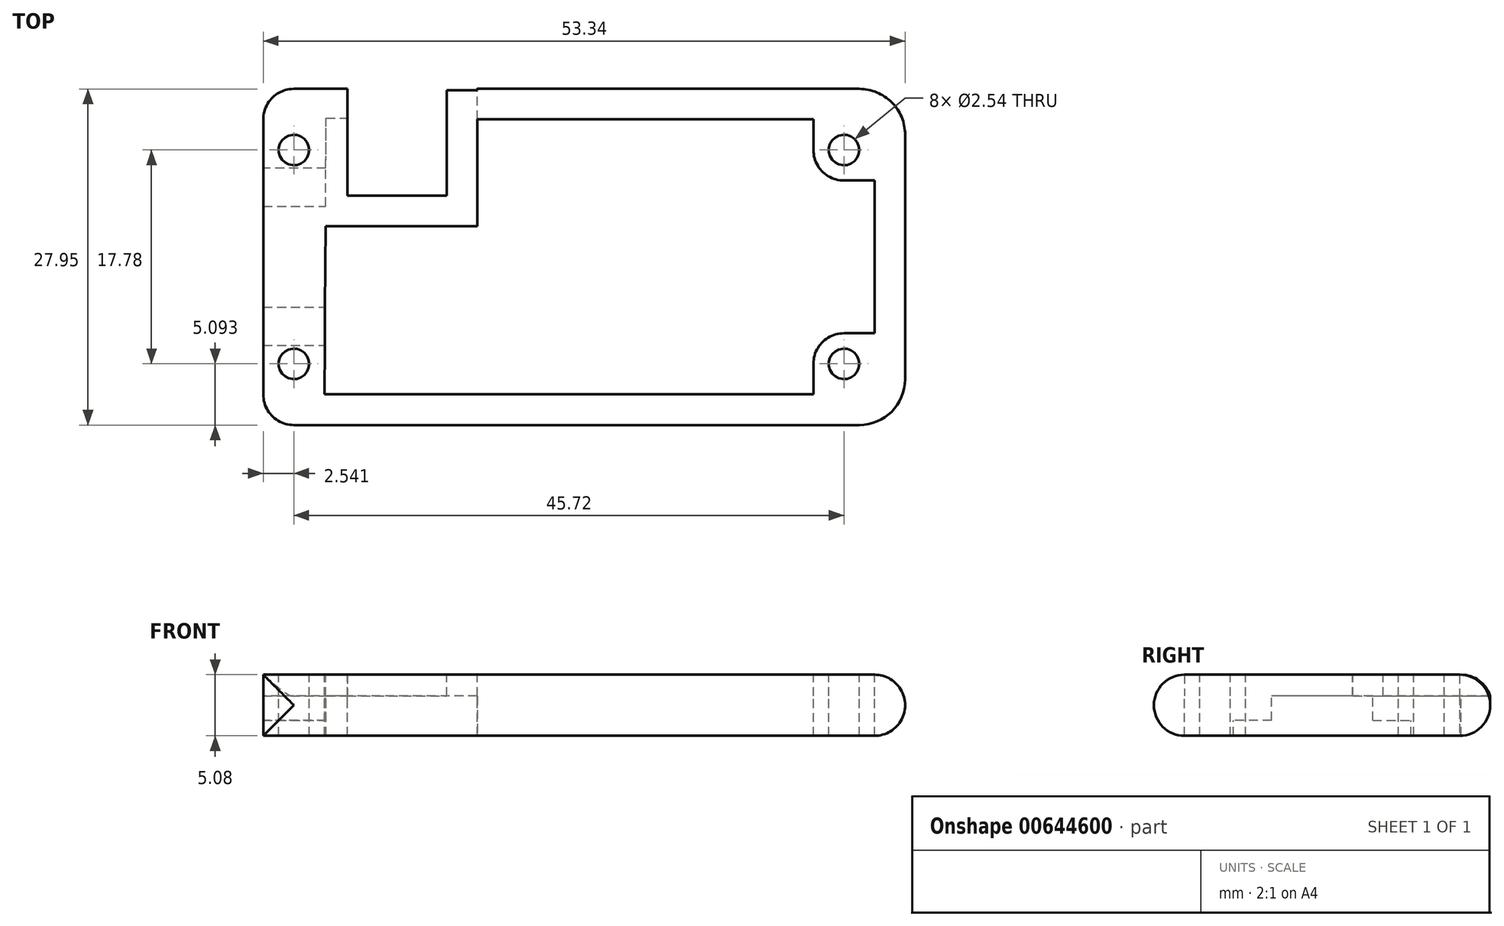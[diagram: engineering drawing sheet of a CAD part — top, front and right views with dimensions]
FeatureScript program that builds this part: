
annotation { "Feature Type Name" : "Feature", "Feature Type Description" : "" }
export const myFeature = defineFeature(function(context is Context, id is Id, definition is map)
    precondition{}
    {
        {
            var Q0;
            Q0=qCreatedBy(makeId("Top.planeOp"),FACE);
            var sketch = newSketch(context, id + "F0", { "sketchPlane" : qUnion([Q0])});
            skLineSegment(sketch, "E0", {"start": v(-27.7, 10.58) * mm, "end": v(-27.7, -12.28) * mm});
            skLineSegment(sketch, "E1", {"start": v(-25.17, -14.82) * mm, "end": v(21.82, -14.82) * mm});
            skLineSegment(sketch, "E2", {"start": v(-25.17, 13.12) * mm, "end": v(-20.72, 13.12) * mm});
            skLineSegment(sketch, "E3", {"start": v(-20.72, 13.12) * mm, "end": v(-20.72, 4.23) * mm});
            skLineSegment(sketch, "E4", {"start": v(-20.72, 4.23) * mm, "end": v(-12.47, 4.23) * mm});
            skLineSegment(sketch, "E5", {"start": v(-12.47, 4.23) * mm, "end": v(-12.47, 13.12) * mm});
            skLineSegment(sketch, "E6", {"start": v(23.1, 5.5) * mm, "end": v(23.1, -7.2) * mm});
            skLineSegment(sketch, "E7", {"start": v(18.01, -12.28) * mm, "end": v(-22.63, -12.28) * mm});
            skLineSegment(sketch, "E8", {"start": v(-9.93, 1.7) * mm, "end": v(-9.93, 10.58) * mm});
            skLineSegment(sketch, "E9", {"start": v(18.01, 10.58) * mm, "end": v(-9.93, 10.58) * mm});
            skPoint(sketch, "E10.visualSharp", {"position": v(-27.7, 13.12) * mm});
            skArc(sketch, "E10.filletArc", {"start": v(-25.17, 13.12) * mm, "mid": v(-26.97, 12.38) * mm, "end": v(-27.7, 10.58) * mm});
            skPoint(sketch, "E11.visualSharp", {"position": v(-27.7, -14.82) * mm});
            skArc(sketch, "E11.filletArc", {"start": v(-27.7, -12.28) * mm, "mid": v(-26.97, -14.07) * mm, "end": v(-25.17, -14.82) * mm});
            skPoint(sketch, "E12.visualSharp", {"position": v(25.63, -14.82) * mm});
            skArc(sketch, "E12.filletArc", {"start": v(21.82, -14.82) * mm, "mid": v(24.52, -13.7) * mm, "end": v(25.63, -11) * mm});
            skPoint(sketch, "E13.visualSharp", {"position": v(25.63, 13.12) * mm});
            skArc(sketch, "E13.filletArc", {"start": v(25.63, 9.31) * mm, "mid": v(24.52, 12) * mm, "end": v(21.82, 13.12) * mm});
            skCircle(sketch, "E14", {"center": v(20.55, 8.04) * mm, "radius": 1.27 * mm});
            skCircle(sketch, "E15", {"center": v(20.55, -9.74) * mm, "radius": 1.27 * mm});
            skCircle(sketch, "E16", {"center": v(-25.17, -9.74) * mm, "radius": 1.27 * mm});
            skCircle(sketch, "E17", {"center": v(-25.17, 8.04) * mm, "radius": 1.27 * mm});
            skLineSegment(sketch, "E18", {"start": v(18.01, 10.58) * mm, "end": v(18.01, 8.04) * mm});
            skLineSegment(sketch, "E19", {"start": v(20.55, 5.5) * mm, "end": v(23.1, 5.5) * mm});
            skLineSegment(sketch, "E20", {"start": v(18.01, -12.28) * mm, "end": v(18.01, -9.74) * mm});
            skLineSegment(sketch, "E21", {"start": v(20.55, -7.2) * mm, "end": v(23.1, -7.2) * mm});
            skPoint(sketch, "E22.visualSharp", {"position": v(18.01, -7.2) * mm});
            skArc(sketch, "E22.filletArc", {"start": v(20.55, -7.2) * mm, "mid": v(18.75, -7.94) * mm, "end": v(18.01, -9.74) * mm});
            skPoint(sketch, "E23.visualSharp", {"position": v(18.01, 5.5) * mm});
            skArc(sketch, "E23.filletArc", {"start": v(18.01, 8.04) * mm, "mid": v(18.75, 6.25) * mm, "end": v(20.55, 5.5) * mm});
            skLineSegment(sketch, "E24", {"start": v(-9.83, 1.71) * mm, "end": v(-22.53, 1.7) * mm});
            skLineSegment(sketch, "E25", {"start": v(-22.53, 1.7) * mm, "end": v(-22.63, -12.28) * mm});
            skLineSegment(sketch, "E26", {"start": v(25.63, -11) * mm, "end": v(25.63, 9.31) * mm});
            skLineSegment(sketch, "E27", {"start": v(-12.47, 13.12) * mm, "end": v(21.82, 13.12) * mm});
            skSolve(sketch);
        }
        {
            var Q0;
            Q0=makeQuery(id+"F0.imprint","IMPRINT",FACE,{"disambiguationData":[TD([[makeQuery(id+"F0.imprint","IMPRINT",EDGE,{"derivedFrom":sQuery(id+"F0.wireOp",EDGE,"E0")}),1.0]])]});
            extrude(context, id + "F1", {"entities" : qUnion([Q0]), "oppositeDirection" : true, "depth" : 1.78 * mm, "offsetDistance" : 25.4 * mm});
        }
        {
            var Q0;
            Q0=qCreatedBy(makeId("Top.planeOp"),FACE);
            var sketch = newSketch(context, id + "F2", { "sketchPlane" : qUnion([Q0])});
            skLineSegment(sketch, "E28", {"start": v(23.1, 5.5) * mm, "end": v(23.1, -7.2) * mm});
            skLineSegment(sketch, "E29", {"start": v(18.01, -12.28) * mm, "end": v(-22.63, -12.28) * mm});
            skPoint(sketch, "E30.visualSharp", {"position": v(-27.7, 13.11) * mm});
            skPoint(sketch, "E31.visualSharp", {"position": v(-27.7, -14.83) * mm});
            skPoint(sketch, "E32.visualSharp", {"position": v(25.63, -14.83) * mm});
            skCircle(sketch, "E33", {"center": v(20.55, 8.04) * mm, "radius": 1.27 * mm});
            skCircle(sketch, "E34", {"center": v(20.55, -9.74) * mm, "radius": 1.27 * mm});
            skCircle(sketch, "E35", {"center": v(-25.17, -9.74) * mm, "radius": 1.27 * mm});
            skCircle(sketch, "E36", {"center": v(-25.17, 8.04) * mm, "radius": 1.27 * mm});
            skLineSegment(sketch, "E37", {"start": v(18.01, 10.58) * mm, "end": v(18.01, 8.04) * mm});
            skLineSegment(sketch, "E38", {"start": v(20.55, 5.5) * mm, "end": v(23.1, 5.5) * mm});
            skLineSegment(sketch, "E39", {"start": v(18.01, -12.28) * mm, "end": v(18.01, -9.74) * mm});
            skLineSegment(sketch, "E40", {"start": v(20.55, -7.2) * mm, "end": v(23.1, -7.2) * mm});
            skPoint(sketch, "E41.visualSharp", {"position": v(18.01, -7.2) * mm});
            skArc(sketch, "E41.filletArc", {"start": v(20.55, -7.2) * mm, "mid": v(18.75, -7.94) * mm, "end": v(18.01, -9.74) * mm});
            skPoint(sketch, "E42.visualSharp", {"position": v(18.01, 5.5) * mm});
            skArc(sketch, "E42.filletArc", {"start": v(18.01, 8.04) * mm, "mid": v(18.75, 6.25) * mm, "end": v(20.55, 5.5) * mm});
            skLineSegment(sketch, "E43", {"start": v(-27.7, -5.04) * mm, "end": v(-22.58, -5.04) * mm});
            skLineSegment(sketch, "E44", {"start": v(-22.58, -5.04) * mm, "end": v(-22.63, -12.28) * mm});
            skLineSegment(sketch, "E45", {"start": v(-22.5, 10.69) * mm, "end": v(-20.72, 10.68) * mm});
            skLineSegment(sketch, "E46", {"start": v(-20.72, 10.68) * mm, "end": v(-20.72, 13.11) * mm});
            skLineSegment(sketch, "E47", {"start": v(-27.7, 3.35) * mm, "end": v(-22.53, 3.35) * mm});
            skLineSegment(sketch, "E48", {"start": v(-22.53, 3.35) * mm, "end": v(-22.5, 10.69) * mm});
            skLineSegment(sketch, "E49", {"start": v(18.01, 10.58) * mm, "end": v(-9.93, 10.58) * mm});
            skLineSegment(sketch, "E50", {"start": v(-9.93, 10.58) * mm, "end": v(-9.93, 13.12) * mm});
            skLineSegment(sketch, "E51", {"start": v(-22.51, 6.53) * mm, "end": v(-27.7, 6.53) * mm});
            skLineSegment(sketch, "E52", {"start": v(-27.7, -5.04) * mm, "end": v(-27.7, -8.21) * mm});
            skLineSegment(sketch, "E53", {"start": v(-27.7, -8.21) * mm, "end": v(-22.6, -8.21) * mm});
            skLineSegment(sketch, "E54", {"start": v(-27.7, 3.35) * mm, "end": v(-27.7, 10.57) * mm});
            skLineSegment(sketch, "E55", {"start": v(-20.72, 13.11) * mm, "end": v(-25.17, 13.11) * mm});
            skArc(sketch, "E56.filletArc", {"start": v(-25.17, 13.11) * mm, "mid": v(-26.97, 12.37) * mm, "end": v(-27.7, 10.57) * mm});
            skLineSegment(sketch, "E57", {"start": v(-27.7, -5.04) * mm, "end": v(-27.7, -12.29) * mm});
            skArc(sketch, "E58.filletArc", {"start": v(-27.7, -12.29) * mm, "mid": v(-26.97, -14.09) * mm, "end": v(-25.17, -14.83) * mm});
            skLineSegment(sketch, "E59", {"start": v(25.63, 10.58) * mm, "end": v(25.63, 10.58) * mm});
            skLineSegment(sketch, "E60", {"start": v(23.08, 13.12) * mm, "end": v(23.1, 13.12) * mm});
            skPoint(sketch, "E61.visualSharp", {"position": v(25.63, 13.12) * mm});
            skLineSegment(sketch, "E62", {"start": v(-25.17, -14.83) * mm, "end": v(21.82, -14.83) * mm});
            skLineSegment(sketch, "E63", {"start": v(25.63, -11.02) * mm, "end": v(25.63, 9.31) * mm});
            skLineSegment(sketch, "E64", {"start": v(21.82, 13.12) * mm, "end": v(-9.93, 13.12) * mm});
            skArc(sketch, "E65.filletArc", {"start": v(21.82, -14.83) * mm, "mid": v(24.52, -13.71) * mm, "end": v(25.63, -11.02) * mm});
            skArc(sketch, "E66.filletArc", {"start": v(25.63, 9.31) * mm, "mid": v(24.52, 12) * mm, "end": v(21.82, 13.12) * mm});
            skSolve(sketch);
        }
        {
            var Q0;
            Q0=makeQuery(id+"F2.imprint","IMPRINT",FACE,{"disambiguationData":[TD([[makeQuery(id+"F2.imprint","IMPRINT",EDGE,{"derivedFrom":sQuery(id+"F2.wireOp",EDGE,"E28")}),1.0]])]});
            var Q1;
            Q1=makeQuery(id+"F2.imprint","IMPRINT",FACE,{"disambiguationData":[TD([[makeQuery(id+"F2.imprint","IMPRINT",EDGE,{"derivedFrom":sQuery(id+"F2.wireOp",EDGE,"E36")}),-1.0]])]});
            extrude(context, id + "F3", {"entities" : qUnion([Q0, Q1]), "operationType" : NewBodyOperationType.ADD, "oppositeDirection" : true, "depth" : 5.08 * mm, "offsetDistance" : 25.4 * mm});
        }
        {
            var Q0;
            {var subQ0=sQuery(id+"F2.wireOp",EDGE,"E47");Q0=makeQuery(id+"F2.imprint","IMPRINT",FACE,{"disambiguationData":[TD([[makeQuery(id+"F2.imprint","IMPRINT",EDGE,{"derivedFrom":subQ0}),1.0]])]});}
            var Q1;
            {var subQ0=sQuery(id+"F2.wireOp",EDGE,"E43");Q1=makeQuery(id+"F2.imprint","IMPRINT",FACE,{"disambiguationData":[TD([[makeQuery(id+"F2.imprint","IMPRINT",EDGE,{"derivedFrom":subQ0}),-1.0]])]});}
            extrude(context, id + "F4", {"entities" : qUnion([Q0, Q1]), "operationType" : NewBodyOperationType.ADD, "oppositeDirection" : true, "depth" : 3.8 * mm, "offsetDistance" : 25.4 * mm});
        }
        {
            var Q0;
            Q0=makeQuery(id+"F3.opExtrude","CAP_EDGE",EDGE,{"disambiguationData":[OSD([sQuery(id+"F2.wireOp",EDGE,"E62")])],"isStart":false});
            var Q1;
            Q1=makeQuery(id+"F3.opExtrude","CAP_EDGE",EDGE,{"disambiguationData":[OSD([sQuery(id+"F2.wireOp",EDGE,"E62")])],"isStart":true});
            var Q2;
            Q2=makeQuery(id+"F3.opExtrude","CAP_EDGE",EDGE,{"disambiguationData":[OSD([sQuery(id+"F2.wireOp",EDGE,"E63")])],"isStart":false});
            var Q3;
            Q3=makeQuery(id+"F3.opExtrude","CAP_EDGE",EDGE,{"disambiguationData":[OSD([sQuery(id+"F2.wireOp",EDGE,"E64")])],"isStart":false});
            var Q4;
            Q4=makeQuery(id+"F3.opExtrude","CAP_EDGE",EDGE,{"disambiguationData":[OSD([sQuery(id+"F2.wireOp",EDGE,"E65.filletArc")])],"isStart":true});
            var Q5;
            Q5=makeQuery(id+"F1.opExtrude","CAP_EDGE",EDGE,{"disambiguationData":[OSD([sQuery(id+"F0.wireOp",EDGE,"E13.filletArc")])],"isStart":true});
            var Q6;
            Q6=makeQuery(id+"F3.opExtrude","CAP_EDGE",EDGE,{"disambiguationData":[OSD([sQuery(id+"F2.wireOp",EDGE,"E55")])],"isStart":false});
            var Q7;
            Q7=makeQuery(id+"F1.opExtrude","CAP_EDGE",EDGE,{"disambiguationData":[OSD([sQuery(id+"F0.wireOp",EDGE,"E2")])],"isStart":true});
            fillet(context, id + "F5", {"entities" : qUnion([Q0, Q1, Q2, Q3, Q4, Q5, Q6, Q7]), "radius" : 2.54 * mm, "allowEdgeOverflow" : false});
        }
    });
